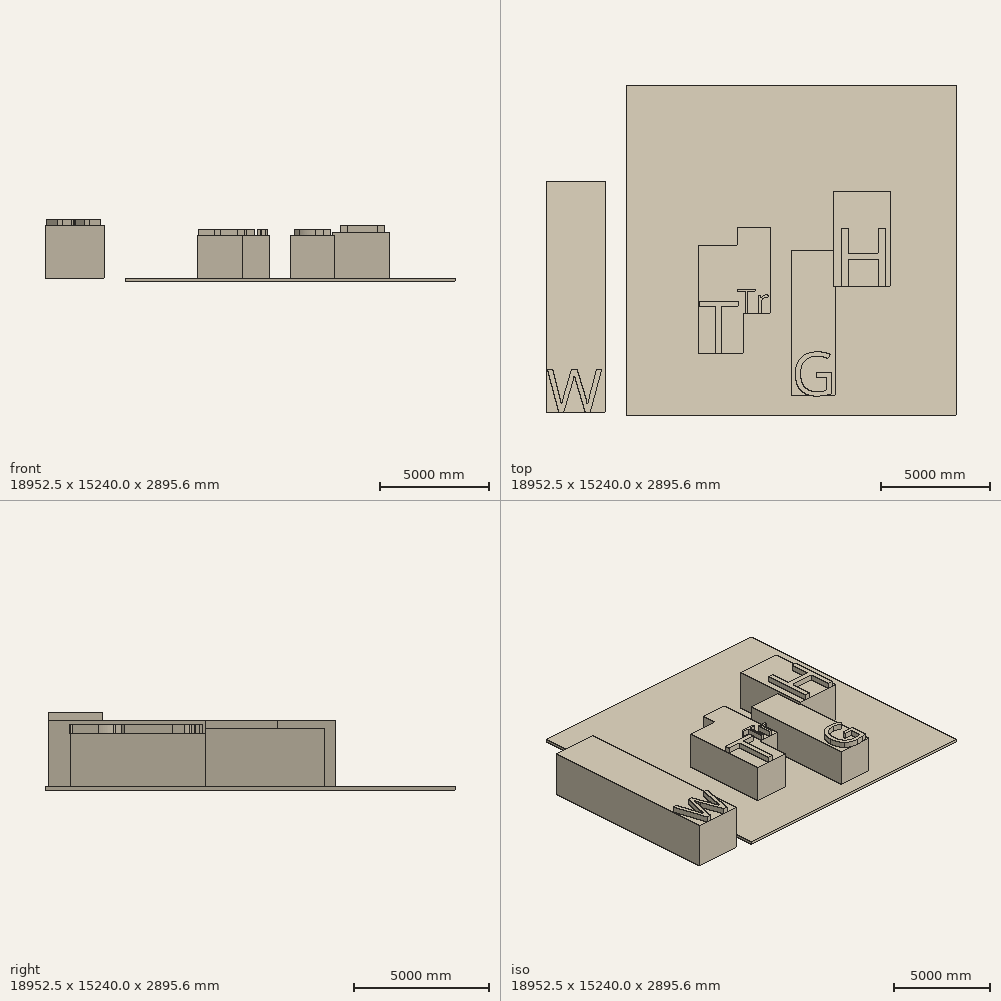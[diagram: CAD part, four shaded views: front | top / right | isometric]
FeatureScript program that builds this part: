
annotation { "Feature Type Name" : "Feature", "Feature Type Description" : "" }
export const myFeature = defineFeature(function(context is Context, id is Id, definition is map)
    precondition{}
    {
        {
            var Q0;
            Q0=qCreatedBy(makeId("Top.planeOp"),FACE);
            var sketch = newSketch(context, id + "F0", { "sketchPlane" : qUnion([Q0])});
            skLineSegment(sketch, "E0.bottom", {"start": v(-7620, 7620) * mm, "end": v(7620, 7620) * mm});
            skLineSegment(sketch, "E0.top", {"start": v(-7620, -7620) * mm, "end": v(7620, -7620) * mm});
            skLineSegment(sketch, "E0.left", {"start": v(-7620, 7620) * mm, "end": v(-7620, -7620) * mm});
            skLineSegment(sketch, "E0.right", {"start": v(7620, 7620) * mm, "end": v(7620, -7620) * mm});
            skPoint(sketch, "E0.middle", {"position": v(0, 0) * mm});
            skLineSegment(sketch, "E1", {"start": v(-7620, 7620) * mm, "end": v(-7620, 7010.4) * mm, "construction": true});
            skLineSegment(sketch, "E2.0", {"start": v(-7010.4, 7010.4) * mm, "end": v(-7010.4, -7010.4) * mm, "construction": true});
            skLineSegment(sketch, "E2.1", {"start": v(-7010.4, 7010.4) * mm, "end": v(7010.4, 7010.4) * mm, "construction": true});
            skLineSegment(sketch, "E2.2", {"start": v(7010.4, 7010.4) * mm, "end": v(7010.4, -7010.4) * mm, "construction": true});
            skLineSegment(sketch, "E2.3", {"start": v(-7010.4, -7010.4) * mm, "end": v(7010.4, -7010.4) * mm, "construction": true});
            skSolve(sketch);
        }
        {
            var Q0;
            Q0 = qSketchRegion(id + "F0", true);
            extrude(context, id + "F1", {"entities" : qUnion([Q0]), "depth" : 152.4 * mm});
        }
        {
            var Q0;
            Q0=qCreatedBy(makeId("Top.planeOp"),FACE);
            var sketch = newSketch(context, id + "F2", { "sketchPlane" : qUnion([Q0])});
            skLineSegment(sketch, "E3.bottom", {"start": v(0, 0) * mm, "end": v(2011.68, 0) * mm});
            skLineSegment(sketch, "E3.top", {"start": v(0, -6705.6) * mm, "end": v(2011.68, -6705.6) * mm});
            skLineSegment(sketch, "E3.left", {"start": v(0, 0) * mm, "end": v(0, -6705.6) * mm});
            skLineSegment(sketch, "E3.right", {"start": v(2011.68, 0) * mm, "end": v(2011.68, -6705.6) * mm});
            skSolve(sketch);
        }
        {
            var Q0;
            Q0=makeQuery(id+"F2.imprint","IMPRINT",FACE,{"disambiguationData":[TD([[makeQuery(id+"F2.imprint","IMPRINT",EDGE,{"derivedFrom":sQuery(id+"F2.wireOp",EDGE,"E3.bottom")}),-1.0]])]});
            var Q1;
            Q1=sQuery(id+"F2.wireOp",EDGE,"E3.left");
            var Q2;
            Q2=sQuery(id+"F2.wireOp",EDGE,"E3.bottom");
            var Q3;
            Q3=sQuery(id+"F2.wireOp",EDGE,"E3.right");
            var Q4;
            Q4=sQuery(id+"F2.wireOp",EDGE,"E3.top");
            extrude(context, id + "F3", {"entities" : qUnion([Q0]), "surfaceEntities" : qUnion([Q1, Q2, Q3, Q4]), "depth" : 2133.6 * mm});
        }
        {
            var Q0;
            Q0=makeQuery(id+"F3.opExtrude","CAP_FACE",FACE,{"disambiguationData":[OSD([sQuery(id+"F2.wireOp",EDGE,"E3.bottom"),sQuery(id+"F2.wireOp",EDGE,"E3.top"),sQuery(id+"F2.wireOp",EDGE,"E3.left"),sQuery(id+"F2.wireOp",EDGE,"E3.right")])],"isStart":false});
            var sketch = newSketch(context, id + "F4", { "sketchPlane" : qUnion([Q0])});
            skText(sketch, "E4", { "text": "G", "fontName": "OpenSans-Regular.ttf"});
            const initialGuessF4  = {"E4": [0, -6.7056, 1, 0, 2.01255]};
            skSetInitialGuess(sketch, initialGuessF4);
            skSolve(sketch);
        }
        {
            var Q0;
            Q0 = qSketchRegion(id + "F4", true);
            extrude(context, id + "F5", {"entities" : qUnion([Q0]), "operationType" : NewBodyOperationType.ADD, "depth" : 304.8 * mm});
        }
        {
            var Q0;
            Q0=makeQuery(id+"F2.imprint","IMPRINT",FACE,{"disambiguationData":[TD([[makeQuery(id+"F2.imprint","IMPRINT",EDGE,{"derivedFrom":sQuery(id+"F2.wireOp",EDGE,"E3.bottom")}),-1.0]])]});
            var sketch = newSketch(context, id + "F6", { "sketchPlane" : qUnion([Q0])});
            skLineSegment(sketch, "E5.bottom", {"start": v(-4305.78, 214.78) * mm, "end": v(-2233.14, 214.78) * mm});
            skLineSegment(sketch, "E5.top", {"start": v(-4305.78, -4783.94) * mm, "end": v(-2233.14, -4783.94) * mm});
            skLineSegment(sketch, "E5.left", {"start": v(-4305.78, 214.78) * mm, "end": v(-4305.78, -4783.94) * mm});
            skLineSegment(sketch, "E5.right", {"start": v(-2233.14, 214.78) * mm, "end": v(-2233.14, -4783.94) * mm});
            skSolve(sketch);
        }
        {
            var Q0;
            Q0 = qSketchRegion(id + "F6", true);
            extrude(context, id + "F7", {"entities" : qUnion([Q0]), "depth" : 2133.6 * mm});
        }
        {
            var Q0;
            Q0=makeQuery(id+"F7.opExtrude","CAP_FACE",FACE,{"disambiguationData":[OSD([sQuery(id+"F6.wireOp",EDGE,"E5.bottom"),sQuery(id+"F6.wireOp",EDGE,"E5.top"),sQuery(id+"F6.wireOp",EDGE,"E5.left"),sQuery(id+"F6.wireOp",EDGE,"E5.right")])],"isStart":false});
            var sketch = newSketch(context, id + "F8", { "sketchPlane" : qUnion([Q0])});
            skText(sketch, "E6", { "text": "T", "fontName": "OpenSans-Regular.ttf"});
            const initialGuessF8  = {"E6": [-4.30578, -4.78394, 1, 0, 2.45142]};
            skSetInitialGuess(sketch, initialGuessF8);
            skSolve(sketch);
        }
        {
            var Q0;
            Q0 = qSketchRegion(id + "F8", true);
            extrude(context, id + "F9", {"entities" : qUnion([Q0]), "operationType" : NewBodyOperationType.ADD, "depth" : 304.8 * mm});
        }
        {
            var Q0;
            Q0=qCreatedBy(makeId("Top.planeOp"),FACE);
            var sketch = newSketch(context, id + "F10", { "sketchPlane" : qUnion([Q0])});
            skLineSegment(sketch, "E7.bottom", {"start": v(-2510.78, 1070.76) * mm, "end": v(-956.3, 1070.76) * mm});
            skLineSegment(sketch, "E7.top", {"start": v(-2510.78, -2891.64) * mm, "end": v(-956.3, -2891.64) * mm});
            skLineSegment(sketch, "E7.left", {"start": v(-2510.78, 1070.76) * mm, "end": v(-2510.78, -2891.64) * mm});
            skLineSegment(sketch, "E7.right", {"start": v(-956.3, 1070.76) * mm, "end": v(-956.3, -2891.64) * mm});
            skSolve(sketch);
        }
        {
            var Q0;
            Q0=makeQuery(id+"F10.imprint","IMPRINT",FACE,{"disambiguationData":[TD([[makeQuery(id+"F10.imprint","IMPRINT",EDGE,{"derivedFrom":sQuery(id+"F10.wireOp",EDGE,"E7.bottom")}),-1.0]])]});
            extrude(context, id + "F11", {"entities" : qUnion([Q0]), "depth" : 2133.6 * mm});
        }
        {
            var Q0;
            Q0=makeQuery(id+"F11.opExtrude","CAP_FACE",FACE,{"disambiguationData":[OSD([sQuery(id+"F10.wireOp",EDGE,"E7.bottom"),sQuery(id+"F10.wireOp",EDGE,"E7.top"),sQuery(id+"F10.wireOp",EDGE,"E7.left"),sQuery(id+"F10.wireOp",EDGE,"E7.right")])],"isStart":false});
            var sketch = newSketch(context, id + "F12", { "sketchPlane" : qUnion([Q0])});
            skText(sketch, "E8", { "text": "Tr", "fontName": "OpenSans-Regular.ttf"});
            const initialGuessF12  = {"E8": [-2.51078, -2.89164, 1, 0, 1.10575]};
            skSetInitialGuess(sketch, initialGuessF12);
            skSolve(sketch);
        }
        {
            var Q0;
            Q0 = qSketchRegion(id + "F12", true);
            extrude(context, id + "F13", {"entities" : qUnion([Q0]), "operationType" : NewBodyOperationType.ADD, "depth" : 304.8 * mm});
        }
        {
            var Q0;
            Q0=makeQuery(id+"F1.opExtrude","CAP_FACE",FACE,{"disambiguationData":[OSD([sQuery(id+"F0.wireOp",EDGE,"E0.bottom"),sQuery(id+"F0.wireOp",EDGE,"E0.top"),sQuery(id+"F0.wireOp",EDGE,"E0.left"),sQuery(id+"F0.wireOp",EDGE,"E0.right")])],"isStart":false});
            var sketch = newSketch(context, id + "F14", { "sketchPlane" : qUnion([Q0])});
            skLineSegment(sketch, "E9.bottom", {"start": v(1939.8, 2747.36) * mm, "end": v(4591.56, 2747.36) * mm});
            skLineSegment(sketch, "E9.top", {"start": v(1939.8, -1672.24) * mm, "end": v(4591.56, -1672.24) * mm});
            skLineSegment(sketch, "E9.left", {"start": v(1939.8, 2747.36) * mm, "end": v(1939.8, -1672.24) * mm});
            skLineSegment(sketch, "E9.right", {"start": v(4591.56, 2747.36) * mm, "end": v(4591.56, -1672.24) * mm});
            skSolve(sketch);
        }
        {
            var Q0;
            Q0 = qSketchRegion(id + "F14", true);
            var Q1;
            Q1=makeQuery(id+"F14.imprint","IMPRINT",FACE,{"disambiguationData":[TD([[makeQuery(id+"F14.imprint","IMPRINT",EDGE,{"derivedFrom":sQuery(id+"F14.wireOp",EDGE,"E9.bottom")}),-1.0]])]});
            extrude(context, id + "F15", {"entities" : qUnion([Q0, Q1]), "depth" : 2133.6 * mm});
        }
        {
            var Q0;
            Q0=makeQuery(id+"F15.opExtrude","CAP_FACE",FACE,{"disambiguationData":[OSD([sQuery(id+"F14.wireOp",EDGE,"E9.bottom"),sQuery(id+"F14.wireOp",EDGE,"E9.top"),sQuery(id+"F14.wireOp",EDGE,"E9.left"),sQuery(id+"F14.wireOp",EDGE,"E9.right")])],"isStart":false});
            var sketch = newSketch(context, id + "F16", { "sketchPlane" : qUnion([Q0])});
            skText(sketch, "E10", { "text": "H", "fontName": "OpenSans-Regular.ttf"});
            const initialGuessF16  = {"E10": [1.9398, -1.67224, 1, 0, 2.70818]};
            skSetInitialGuess(sketch, initialGuessF16);
            skSolve(sketch);
        }
        {
            var Q0;
            Q0 = qSketchRegion(id + "F16", true);
            extrude(context, id + "F17", {"entities" : qUnion([Q0]), "operationType" : NewBodyOperationType.ADD, "depth" : 304.8 * mm});
        }
        {
            var Q0;
            Q0=makeQuery(id+"F1.opExtrude","CAP_FACE",FACE,{"disambiguationData":[OSD([sQuery(id+"F0.wireOp",EDGE,"E0.bottom"),sQuery(id+"F0.wireOp",EDGE,"E0.top"),sQuery(id+"F0.wireOp",EDGE,"E0.left"),sQuery(id+"F0.wireOp",EDGE,"E0.right")])],"isStart":false});
            var sketch = newSketch(context, id + "F18", { "sketchPlane" : qUnion([Q0])});
            skLineSegment(sketch, "E11.bottom", {"start": v(-11332.55, 3176.53) * mm, "end": v(-8589.35, 3176.53) * mm});
            skLineSegment(sketch, "E11.top", {"start": v(-11332.55, -7491.47) * mm, "end": v(-8589.35, -7491.47) * mm});
            skLineSegment(sketch, "E11.left", {"start": v(-11332.55, 3176.53) * mm, "end": v(-11332.55, -7491.47) * mm});
            skLineSegment(sketch, "E11.right", {"start": v(-8589.35, 3176.53) * mm, "end": v(-8589.35, -7491.47) * mm});
            skSolve(sketch);
        }
        {
            var Q0;
            Q0 = qSketchRegion(id + "F18", true);
            var Q1;
            Q1=makeQuery(id+"F18.imprint","IMPRINT",FACE,{"disambiguationData":[TD([[makeQuery(id+"F18.imprint","IMPRINT",EDGE,{"derivedFrom":sQuery(id+"F18.wireOp",EDGE,"E11.bottom")}),-1.0]])]});
            extrude(context, id + "F19", {"entities" : qUnion([Q0, Q1]), "depth" : 2438.4 * mm});
        }
        {
            var Q0;
            Q0=makeQuery(id+"F19.opExtrude","CAP_FACE",FACE,{"disambiguationData":[OSD([sQuery(id+"F18.wireOp",EDGE,"E11.bottom"),sQuery(id+"F18.wireOp",EDGE,"E11.top"),sQuery(id+"F18.wireOp",EDGE,"E11.left"),sQuery(id+"F18.wireOp",EDGE,"E11.right")])],"isStart":false});
            var sketch = newSketch(context, id + "F20", { "sketchPlane" : qUnion([Q0])});
            skText(sketch, "E12", { "text": "W", "fontName": "OpenSans-Regular.ttf"});
            const initialGuessF20  = {"E12": [-11.33255, -7.49147, 1, 0, 2.02154]};
            skSetInitialGuess(sketch, initialGuessF20);
            skSolve(sketch);
        }
        {
            var Q0;
            Q0 = qSketchRegion(id + "F20", true);
            extrude(context, id + "F21", {"entities" : qUnion([Q0]), "operationType" : NewBodyOperationType.ADD, "depth" : 304.8 * mm});
        }
    });
